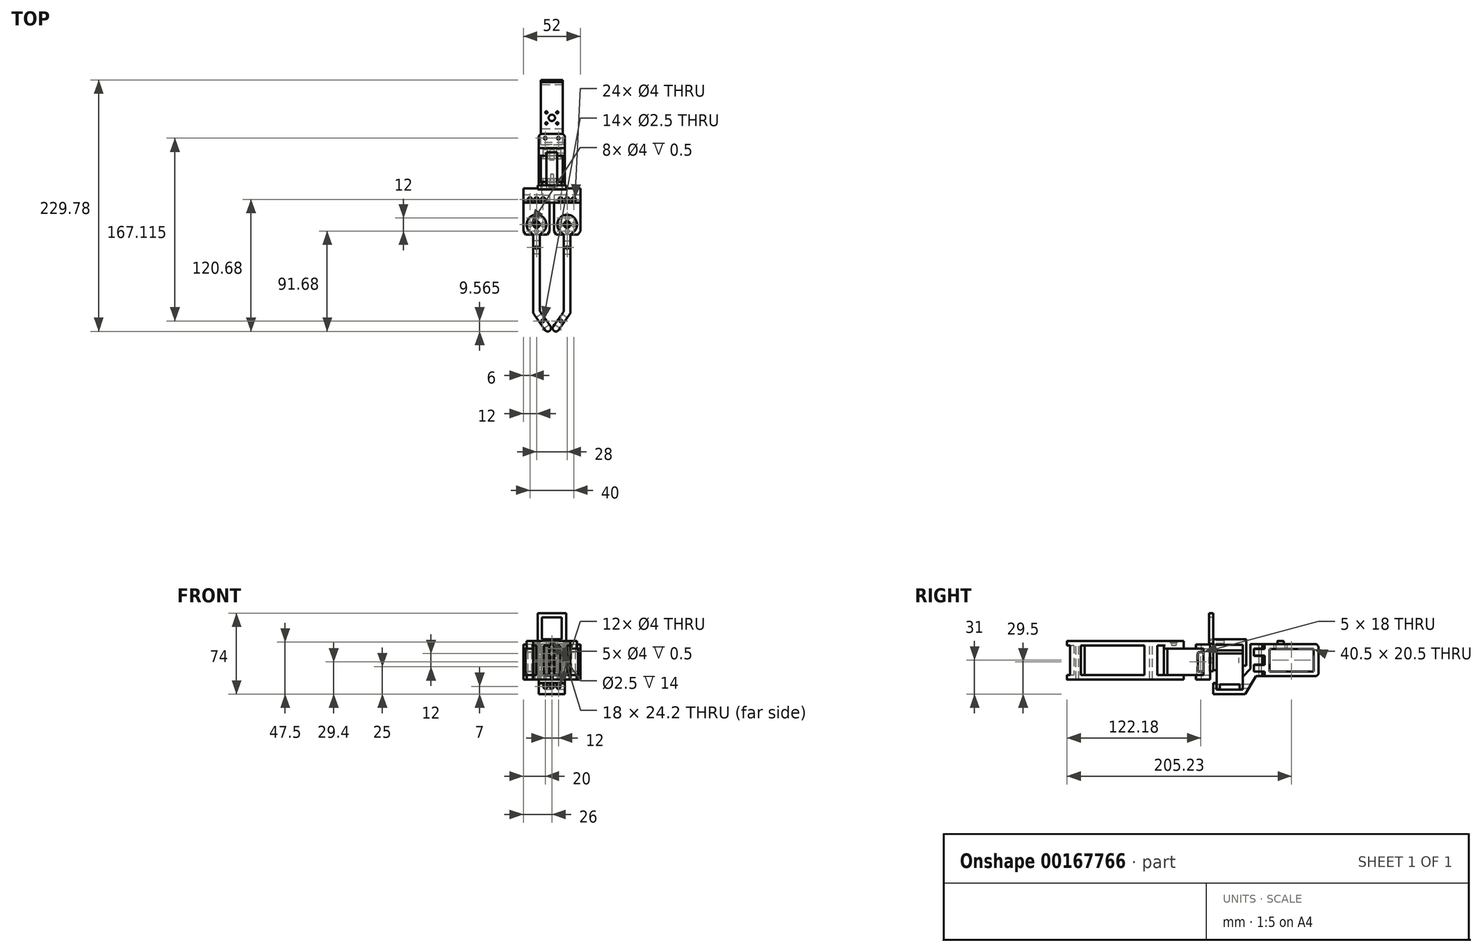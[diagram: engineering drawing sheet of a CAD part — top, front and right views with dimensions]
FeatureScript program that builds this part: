
annotation { "Feature Type Name" : "Feature", "Feature Type Description" : "" }
export const myFeature = defineFeature(function(context is Context, id is Id, definition is map)
    precondition{}
    {
        {
            var Q0;
            Q0=qCreatedBy(makeId("Right.planeOp"),FACE);
            var sketch = newSketch(context, id + "F0", { "sketchPlane" : qUnion([Q0])});
            skLineSegment(sketch, "E0.bottom", {"start": v(30.25, 10.25) * mm, "end": v(-10.25, 10.25) * mm});
            skLineSegment(sketch, "E0.top", {"start": v(30.25, -10.25) * mm, "end": v(-10.25, -10.25) * mm});
            skLineSegment(sketch, "E0.left", {"start": v(30.25, 10.25) * mm, "end": v(30.25, -10.25) * mm});
            skLineSegment(sketch, "E0.right", {"start": v(-10.25, 10.25) * mm, "end": v(-10.25, -10.25) * mm});
            skLineSegment(sketch, "E1.bottom", {"start": v(-14.55, 14.55) * mm, "end": v(34.55, 14.55) * mm});
            skLineSegment(sketch, "E1.top", {"start": v(-14.55, -14.55) * mm, "end": v(34.55, -14.55) * mm});
            skLineSegment(sketch, "E1.left", {"start": v(-14.55, 14.55) * mm, "end": v(-14.55, -14.55) * mm});
            skLineSegment(sketch, "E1.right", {"start": v(34.55, 14.55) * mm, "end": v(34.55, -14.55) * mm});
            skLineSegment(sketch, "E2", {"start": v(10, 14.55) * mm, "end": v(10, 10.25) * mm, "construction": true});
            skLineSegment(sketch, "E3", {"start": v(30.25, 0) * mm, "end": v(34.55, 0) * mm, "construction": true});
            skLineSegment(sketch, "E4", {"start": v(-10.25, 0) * mm, "end": v(10.25, 0) * mm, "construction": true});
            skSolve(sketch);
        }
        {
            var Q0;
            Q0=qSketchRegion(id+"F0",true);
            extrude(context, id + "F1", {"entities" : qUnion([Q0]), "endBound" : BoundingType.SYMMETRIC, "depth" : 20 * mm});
        }
        {
            var Q0;
            Q0=makeQuery(id+"F1.opExtrude","SWEPT_EDGE",EDGE,{"disambiguationData":[OSD([sQuery(id+"F0.wireOp",EDGE,"E1.bottom"),sQuery(id+"F0.wireOp",EDGE,"E1.right")])]});
            var Q1;
            Q1=makeQuery(id+"F1.opExtrude","SWEPT_EDGE",EDGE,{"disambiguationData":[OSD([sQuery(id+"F0.wireOp",EDGE,"E1.top"),sQuery(id+"F0.wireOp",EDGE,"E1.right")])]});
            chamfer(context, id + "F2", {"entities" : qUnion([Q0, Q1]), "width" : 2 * mm, "tangentPropagation" : true});
        }
        {
            var Q0;
            Q0=makeQuery(id+"F1.opExtrude","SWEPT_FACE",FACE,{"disambiguationData":[OSD([sQuery(id+"F0.wireOp",EDGE,"E1.bottom")])]});
            var sketch = newSketch(context, id + "F3", { "sketchPlane" : qUnion([Q0])});
            skCircle(sketch, "E5", {"center": v(0, 0) * mm, "radius": 2.9 * mm});
            skSolve(sketch);
        }
        {
            var Q0;
            Q0=qSketchRegion(id+"F3",true);
            extrude(context, id + "F4", {"entities" : qUnion([Q0]), "operationType" : NewBodyOperationType.ADD, "depth" : 3 * mm});
        }
        {
            var Q0;
            Q0=makeQuery(id+"F1.opExtrude","SWEPT_FACE",FACE,{"disambiguationData":[OSD([sQuery(id+"F0.wireOp",EDGE,"E1.left")])]});
            var sketch = newSketch(context, id + "F5", { "sketchPlane" : qUnion([Q0])});
            skLineSegment(sketch, "E6.bottom", {"start": v(-10, 10.25) * mm, "end": v(10, 10.25) * mm});
            skLineSegment(sketch, "E6.top", {"start": v(-10, 4.25) * mm, "end": v(10, 4.25) * mm});
            skLineSegment(sketch, "E6.left", {"start": v(-10, 10.25) * mm, "end": v(-10, 4.25) * mm});
            skLineSegment(sketch, "E6.right", {"start": v(10, 10.25) * mm, "end": v(10, 4.25) * mm});
            skLineSegment(sketch, "E7.bottom", {"start": v(-10, -4.25) * mm, "end": v(10, -4.25) * mm});
            skLineSegment(sketch, "E7.top", {"start": v(-10, -10.25) * mm, "end": v(10, -10.25) * mm});
            skLineSegment(sketch, "E7.left", {"start": v(-10, -4.25) * mm, "end": v(-10, -10.25) * mm});
            skLineSegment(sketch, "E7.right", {"start": v(10, -4.25) * mm, "end": v(10, -10.25) * mm});
            skSolve(sketch);
        }
        {
            var Q0;
            Q0=qSketchRegion(id+"F5",true);
            extrude(context, id + "F6", {"entities" : qUnion([Q0]), "operationType" : NewBodyOperationType.ADD, "depth" : 10 * mm});
        }
        {
            var Q0;
            Q0=qCreatedBy(makeId("Top.planeOp"),FACE);
            var sketch = newSketch(context, id + "F7", { "sketchPlane" : qUnion([Q0])});
            skCircle(sketch, "E8", {"center": v(-6, -18.55) * mm, "radius": 1.25 * mm});
            skCircle(sketch, "E9", {"center": v(6, -18.55) * mm, "radius": 1.25 * mm});
            skSolve(sketch);
        }
        {
            var Q0;
            Q0=qSketchRegion(id+"F7",true);
            extrude(context, id + "F8", {"entities" : qUnion([Q0]), "operationType" : NewBodyOperationType.REMOVE, "endBound" : BoundingType.THROUGH_ALL, "oppositeDirection" : true, "depth" : 25 * mm, "hasSecondDirection" : true, "secondDirectionBound" : SecondDirectionBoundingType.THROUGH_ALL, "secondDirectionOppositeDirection" : false, "secondDirectionDepth" : 25 * mm});
        }
        {
            var Q0;
            Q0=makeQuery(id+"F1.opExtrude","SWEPT_FACE",FACE,{"disambiguationData":[OSD([sQuery(id+"F0.wireOp",EDGE,"E1.bottom")])]});
            var sketch = newSketch(context, id + "F9", { "sketchPlane" : qUnion([Q0])});
            skCircle(sketch, "E10", {"center": v(-5, -5) * mm, "radius": 1 * mm});
            skLineSegment(sketch, "E11.bottom", {"start": v(-5, -5) * mm, "end": v(5, -5) * mm, "construction": true});
            skLineSegment(sketch, "E11.top", {"start": v(-5, 5) * mm, "end": v(5, 5) * mm, "construction": true});
            skLineSegment(sketch, "E11.left", {"start": v(-5, -5) * mm, "end": v(-5, 5) * mm, "construction": true});
            skLineSegment(sketch, "E11.right", {"start": v(5, -5) * mm, "end": v(5, 5) * mm, "construction": true});
            skLineSegment(sketch, "E12", {"start": v(-5, 5) * mm, "end": v(5, -5) * mm, "construction": true});
            skCircle(sketch, "E13", {"center": v(-5, 5) * mm, "radius": 1 * mm});
            skCircle(sketch, "E14", {"center": v(5, 5) * mm, "radius": 1 * mm});
            skCircle(sketch, "E15", {"center": v(5, -5) * mm, "radius": 1 * mm});
            skSolve(sketch);
        }
        {
            var Q0;
            Q0=qSketchRegion(id+"F9",true);
            extrude(context, id + "F10", {"entities" : qUnion([Q0]), "operationType" : NewBodyOperationType.REMOVE, "endBound" : BoundingType.UP_TO_NEXT, "oppositeDirection" : true, "depth" : 25 * mm});
        }
        {
            var Q0;
            Q0=qCreatedBy(makeId("Right.planeOp"),FACE);
            var sketch = newSketch(context, id + "F11", { "sketchPlane" : qUnion([Q0])});
            skLineSegment(sketch, "E16.bottom", {"start": v(-34.55, -27) * mm, "end": v(-58.55, -27) * mm});
            skLineSegment(sketch, "E16.top", {"start": v(-34.55, 9) * mm, "end": v(-58.55, 9) * mm});
            skLineSegment(sketch, "E16.left", {"start": v(-34.55, -27) * mm, "end": v(-34.55, 9) * mm});
            skLineSegment(sketch, "E16.right", {"start": v(-58.55, -27) * mm, "end": v(-58.55, 9) * mm});
            skLineSegment(sketch, "E17.bottom", {"start": v(-58.55, -9) * mm, "end": v(-61.55, -9) * mm, "construction": true});
            skLineSegment(sketch, "E17.top", {"start": v(-58.55, 9) * mm, "end": v(-61.55, 9) * mm, "construction": true});
            skLineSegment(sketch, "E17.left", {"start": v(-58.55, -9) * mm, "end": v(-58.55, 9) * mm, "construction": true});
            skLineSegment(sketch, "E17.right", {"start": v(-61.55, -9) * mm, "end": v(-61.55, 9) * mm, "construction": true});
            skLineSegment(sketch, "E18.bottom", {"start": v(-55.55, -27) * mm, "end": v(-37.55, -27) * mm});
            skLineSegment(sketch, "E18.top", {"start": v(-55.55, -22) * mm, "end": v(-37.55, -22) * mm});
            skLineSegment(sketch, "E18.left", {"start": v(-55.55, -27) * mm, "end": v(-55.55, -22) * mm});
            skLineSegment(sketch, "E18.right", {"start": v(-37.55, -27) * mm, "end": v(-37.55, -22) * mm});
            skSolve(sketch);
        }
        {
            var Q0;
            Q0=makeQuery(id+"F11.imprint","IMPRINT",FACE,{"disambiguationData":[TD([[makeQuery(id+"F11.imprint","IMPRINT",EDGE,{"derivedFrom":sQuery(id+"F11.wireOp",EDGE,"E16.top")}),1.0]])]});
            extrude(context, id + "F12", {"entities" : qUnion([Q0]), "endBound" : BoundingType.SYMMETRIC, "depth" : 24 * mm});
        }
        {
            var Q0;
            Q0=makeQuery(id+"F12.opExtrude","SWEPT_FACE",FACE,{"disambiguationData":[OSD([sQuery(id+"F11.wireOp",EDGE,"E16.right")])]});
            var sketch = newSketch(context, id + "F13", { "sketchPlane" : qUnion([Q0])});
            skCircle(sketch, "E19", {"center": v(0, 0) * mm, "radius": 9 * mm});
            skCircle(sketch, "E20", {"center": v(0, 0) * mm, "radius": 6 * mm, "construction": true});
            skCircle(sketch, "E21", {"center": v(0, 6) * mm, "radius": 2 * mm});
            skCircle(sketch, "E22", {"center": v(6, 0) * mm, "radius": 2 * mm});
            skCircle(sketch, "E23", {"center": v(-6, 0) * mm, "radius": 2 * mm});
            skCircle(sketch, "E24", {"center": v(0, -6) * mm, "radius": 2 * mm});
            skSolve(sketch);
        }
        {
            var Q0;
            Q0 = qSketchRegion(id + "F13", true);
            extrude(context, id + "F14", {"entities" : qUnion([Q0]), "operationType" : NewBodyOperationType.ADD, "depth" : 3 * mm});
        }
        {
            var Q0;
            Q0=makeQuery(id+"F12.opExtrude","CAP_EDGE",EDGE,{"disambiguationData":[OSD([sQuery(id+"F11.wireOp",EDGE,"E16.top")])],"isStart":false});
            var Q1;
            Q1=makeQuery(id+"F12.opExtrude","CAP_EDGE",EDGE,{"disambiguationData":[OSD([sQuery(id+"F11.wireOp",EDGE,"E16.top")])],"isStart":true});
            chamfer(context, id + "F15", {"entities" : qUnion([Q0, Q1]), "chamferType" : ChamferType.TWO_OFFSETS, "width1" : 3 * mm, "oppositeDirection" : false, "width2" : 2 * mm, "tangentPropagation" : true});
        }
        {
            var Q0;
            Q0=makeQuery(id+"F12.opExtrude","SWEPT_FACE",FACE,{"disambiguationData":[OSD([sQuery(id+"F11.wireOp",EDGE,"E16.left")])]});
            var sketch = newSketch(context, id + "F16", { "sketchPlane" : qUnion([Q0])});
            skCircle(sketch, "E25", {"center": v(0, 0) * mm, "radius": 2 * mm});
            skSolve(sketch);
        }
        {
            var Q0;
            Q0 = qSketchRegion(id + "F16", true);
            extrude(context, id + "F17", {"entities" : qUnion([Q0]), "operationType" : NewBodyOperationType.REMOVE, "oppositeDirection" : true, "depth" : 4 * mm});
        }
        {
            var Q0;
            Q0=qCreatedBy(makeId("Right.planeOp"),FACE);
            var sketch = newSketch(context, id + "F18", { "sketchPlane" : qUnion([Q0])});
            skLineSegment(sketch, "E26", {"start": v(-14.55, 14.55) * mm, "end": v(-14.55, 10.45) * mm});
            skLineSegment(sketch, "E27", {"start": v(-14.55, 10.45) * mm, "end": v(-24.55, 10.45) * mm});
            skLineSegment(sketch, "E28", {"start": v(-24.55, 10.45) * mm, "end": v(-24.55, 4.05) * mm});
            skLineSegment(sketch, "E29", {"start": v(-24.55, 4.05) * mm, "end": v(-14.55, 4.05) * mm});
            skLineSegment(sketch, "E30", {"start": v(-14.55, 4.05) * mm, "end": v(-14.55, -4.05) * mm});
            skLineSegment(sketch, "E31", {"start": v(-14.55, -4.05) * mm, "end": v(-24.55, -4.05) * mm});
            skLineSegment(sketch, "E32", {"start": v(-24.55, -4.05) * mm, "end": v(-24.55, -10.45) * mm});
            skLineSegment(sketch, "E33", {"start": v(-24.55, -10.45) * mm, "end": v(-14.55, -10.45) * mm});
            skLineSegment(sketch, "E34", {"start": v(-14.55, -10.45) * mm, "end": v(-14.55, -14.55) * mm});
            skLineSegment(sketch, "E35", {"start": v(-14.55, -14.55) * mm, "end": v(-22.55, -14.55) * mm});
            skLineSegment(sketch, "E36", {"start": v(-22.55, -14.55) * mm, "end": v(-32.27, -31) * mm});
            skLineSegment(sketch, "E37", {"start": v(-32.27, -31) * mm, "end": v(-61.75, -31) * mm});
            skLineSegment(sketch, "E38", {"start": v(-61.75, -31) * mm, "end": v(-61.75, -21) * mm});
            skLineSegment(sketch, "E39", {"start": v(-61.75, -21) * mm, "end": v(-58.75, -21) * mm});
            skLineSegment(sketch, "E40", {"start": v(-58.75, -21) * mm, "end": v(-58.75, -27) * mm});
            skLineSegment(sketch, "E41", {"start": v(-58.75, -27) * mm, "end": v(-34.55, -27) * mm});
            skLineSegment(sketch, "E42", {"start": v(-34.55, -27) * mm, "end": v(-34.55, -15) * mm});
            skLineSegment(sketch, "E43", {"start": v(-34.55, -15) * mm, "end": v(-27.55, -8) * mm});
            skLineSegment(sketch, "E44", {"start": v(-27.55, -8) * mm, "end": v(-27.55, 14.55) * mm});
            skLineSegment(sketch, "E45", {"start": v(-27.55, 14.55) * mm, "end": v(-14.55, 14.55) * mm});
            skCircle(sketch, "E46", {"center": v(-34.55, -27) * mm, "radius": 4 * mm, "construction": true});
            skSolve(sketch);
        }
        {
            var Q0;
            Q0 = qSketchRegion(id + "F18", true);
            extrude(context, id + "F19", {"entities" : qUnion([Q0]), "endBound" : BoundingType.SYMMETRIC, "depth" : 24 * mm});
        }
        {
            var Q0;
            Q0=makeQuery(id+"F19.opExtrude","CAP_EDGE",EDGE,{"disambiguationData":[OSD([sQuery(id+"F18.wireOp",EDGE,"E26")])],"isStart":false});
            var Q1;
            Q1=makeQuery(id+"F19.opExtrude","CAP_EDGE",EDGE,{"disambiguationData":[OSD([sQuery(id+"F18.wireOp",EDGE,"E30")])],"isStart":false});
            var Q2;
            Q2=makeQuery(id+"F19.opExtrude","CAP_EDGE",EDGE,{"disambiguationData":[OSD([sQuery(id+"F18.wireOp",EDGE,"E34")])],"isStart":false});
            var Q3;
            Q3=makeQuery(id+"F19.opExtrude","CAP_EDGE",EDGE,{"disambiguationData":[OSD([sQuery(id+"F18.wireOp",EDGE,"E26")])],"isStart":true});
            var Q4;
            Q4=makeQuery(id+"F19.opExtrude","CAP_EDGE",EDGE,{"disambiguationData":[OSD([sQuery(id+"F18.wireOp",EDGE,"E30")])],"isStart":true});
            var Q5;
            Q5=makeQuery(id+"F19.opExtrude","CAP_EDGE",EDGE,{"disambiguationData":[OSD([sQuery(id+"F18.wireOp",EDGE,"E34")])],"isStart":true});
            chamfer(context, id + "F20", {"entities" : qUnion([Q0, Q1, Q2, Q3, Q4, Q5]), "width" : 2 * mm, "tangentPropagation" : true});
        }
        {
            var Q0;
            Q0 = qSketchRegion(id + "F7", true);
            extrude(context, id + "F21", {"entities" : qUnion([Q0]), "operationType" : NewBodyOperationType.REMOVE, "endBound" : BoundingType.THROUGH_ALL, "oppositeDirection" : true, "depth" : 25 * mm, "hasSecondDirection" : true, "secondDirectionBound" : SecondDirectionBoundingType.THROUGH_ALL, "secondDirectionOppositeDirection" : false, "secondDirectionDepth" : 25 * mm});
        }
        {
            var Q0;
            Q0=makeQuery(id+"F19.opExtrude","SWEPT_FACE",FACE,{"disambiguationData":[OSD([sQuery(id+"F18.wireOp",EDGE,"E42")])]});
            var sketch = newSketch(context, id + "F22", { "sketchPlane" : qUnion([Q0])});
            skCircle(sketch, "E47", {"center": v(0, -24) * mm, "radius": 2 * mm});
            skPoint(sketch, "E47.centerSnap0", {"position": v(0, -27) * mm});
            skCircle(sketch, "E48", {"center": v(6, -24) * mm, "radius": 2 * mm});
            skCircle(sketch, "E49", {"center": v(-6, -24) * mm, "radius": 2 * mm});
            skSolve(sketch);
        }
        {
            var Q0;
            Q0 = qSketchRegion(id + "F22", true);
            extrude(context, id + "F23", {"entities" : qUnion([Q0]), "operationType" : NewBodyOperationType.REMOVE, "endBound" : BoundingType.THROUGH_ALL, "oppositeDirection" : true, "depth" : 25 * mm, "hasSecondDirection" : true, "secondDirectionBound" : SecondDirectionBoundingType.THROUGH_ALL, "secondDirectionOppositeDirection" : false, "secondDirectionDepth" : 25 * mm});
        }
        {
            var Q0;
            Q0=qCreatedBy(makeId("Right.planeOp"),FACE);
            var sketch = newSketch(context, id + "F24", { "sketchPlane" : qUnion([Q0])});
            skLineSegment(sketch, "E50", {"start": v(-31.55, 19) * mm, "end": v(-31.55, -5) * mm});
            skLineSegment(sketch, "E51", {"start": v(-31.55, -5) * mm, "end": v(-34.55, -5) * mm});
            skLineSegment(sketch, "E52", {"start": v(-34.55, -5) * mm, "end": v(-34.55, 14) * mm});
            skLineSegment(sketch, "E53", {"start": v(-34.55, 14) * mm, "end": v(-61.55, 14) * mm});
            skLineSegment(sketch, "E54", {"start": v(-61.55, 14) * mm, "end": v(-61.55, 19) * mm});
            skLineSegment(sketch, "E55", {"start": v(-61.55, 19) * mm, "end": v(-31.55, 19) * mm});
            skSolve(sketch);
        }
        {
            var Q0;
            Q0 = qSketchRegion(id + "F24", true);
            extrude(context, id + "F25", {"entities" : qUnion([Q0]), "endBound" : BoundingType.SYMMETRIC, "depth" : 10 * mm});
        }
        {
            var Q0;
            Q0=makeQuery(id+"F25.opExtrude","SWEPT_FACE",FACE,{"disambiguationData":[OSD([sQuery(id+"F24.wireOp",EDGE,"E52")])]});
            var sketch = newSketch(context, id + "F26", { "sketchPlane" : qUnion([Q0])});
            skCircle(sketch, "E56", {"center": v(0, 0) * mm, "radius": 2 * mm});
            skSolve(sketch);
        }
        {
            var Q0;
            Q0 = qSketchRegion(id + "F26", true);
            extrude(context, id + "F27", {"entities" : qUnion([Q0]), "operationType" : NewBodyOperationType.ADD, "depth" : 3.5 * mm});
        }
        {
            var Q0;
            Q0=makeQuery(id+"F25.opExtrude","SWEPT_FACE",FACE,{"disambiguationData":[OSD([sQuery(id+"F24.wireOp",EDGE,"E54")])]});
            var sketch = newSketch(context, id + "F28", { "sketchPlane" : qUnion([Q0])});
            skCircle(sketch, "E57", {"center": v(0, 16.5) * mm, "radius": 1.25 * mm});
            skSolve(sketch);
        }
        {
            var Q0;
            Q0 = qSketchRegion(id + "F28", true);
            extrude(context, id + "F29", {"entities" : qUnion([Q0]), "operationType" : NewBodyOperationType.REMOVE, "oppositeDirection" : true, "depth" : 10 * mm});
        }
        {
            var Q0;
            Q0=makeQuery(id+"F25.opExtrude","CAP_EDGE",EDGE,{"disambiguationData":[OSD([sQuery(id+"F24.wireOp",EDGE,"E51")])],"isStart":false});
            var Q1;
            Q1=makeQuery(id+"F25.opExtrude","CAP_EDGE",EDGE,{"disambiguationData":[OSD([sQuery(id+"F24.wireOp",EDGE,"E51")])],"isStart":true});
            fillet(context, id + "F30", {"entities" : qUnion([Q0, Q1]), "radius" : 5 * mm, "tangentPropagation" : true});
        }
        {
            var Q0;
            Q0=makeQuery(id+"F14.opExtrude","CAP_FACE",FACE,{"disambiguationData":[OSD([sQuery(id+"F13.wireOp",EDGE,"E19"),sQuery(id+"F13.wireOp",EDGE,"E21"),sQuery(id+"F13.wireOp",EDGE,"E22"),sQuery(id+"F13.wireOp",EDGE,"E23"),sQuery(id+"F13.wireOp",EDGE,"E24")])],"isStart":false});
            var sketch = newSketch(context, id + "F31", { "sketchPlane" : qUnion([Q0])});
            skLineSegment(sketch, "E58.0", {"start": v(5, 19) * mm, "end": v(-5, 19) * mm});
            skLineSegment(sketch, "E59", {"start": v(-5, 19) * mm, "end": v(-5, 9.14) * mm});
            skLineSegment(sketch, "E60", {"start": v(-5, 9.14) * mm, "end": v(-10, 4.14) * mm});
            skLineSegment(sketch, "E61", {"start": v(-10, 4.14) * mm, "end": v(-10, -10) * mm});
            skLineSegment(sketch, "E62", {"start": v(-10, -10) * mm, "end": v(10, -10) * mm});
            skLineSegment(sketch, "E63", {"start": v(10, -10) * mm, "end": v(10, 4.14) * mm});
            skLineSegment(sketch, "E64", {"start": v(10, 4.14) * mm, "end": v(5, 9.14) * mm});
            skLineSegment(sketch, "E65", {"start": v(5, 9.14) * mm, "end": v(5, 19) * mm});
            skCircle(sketch, "E66", {"center": v(0, 0) * mm, "radius": 10 * mm, "construction": true});
            skCircle(sketch, "E67.0", {"center": v(0, 16.5) * mm, "radius": 1.25 * mm});
            skCircle(sketch, "E68", {"center": v(0, 0) * mm, "radius": 2 * mm});
            skSolve(sketch);
        }
        {
            var Q0;
            Q0 = qSketchRegion(id + "F31", true);
            extrude(context, id + "F32", {"entities" : qUnion([Q0]), "depth" : 4 * mm});
        }
        {
            var Q0;
            Q0=makeQuery(id+"F32.opExtrude","SWEPT_EDGE",EDGE,{"disambiguationData":[OSD([sQuery(id+"F31.wireOp",EDGE,"E62"),sQuery(id+"F31.wireOp",EDGE,"E63")])]});
            var Q1;
            Q1=makeQuery(id+"F32.opExtrude","SWEPT_EDGE",EDGE,{"disambiguationData":[OSD([sQuery(id+"F31.wireOp",EDGE,"E61"),sQuery(id+"F31.wireOp",EDGE,"E62")])]});
            var Q2;
            Q2=makeQuery(id+"F32.opExtrude","SWEPT_EDGE",EDGE,{"disambiguationData":[OSD([sQuery(id+"F31.wireOp",EDGE,"E63"),sQuery(id+"F31.wireOp",EDGE,"E64")])]});
            var Q3;
            Q3=makeQuery(id+"F32.opExtrude","SWEPT_EDGE",EDGE,{"disambiguationData":[OSD([sQuery(id+"F31.wireOp",EDGE,"E60"),sQuery(id+"F31.wireOp",EDGE,"E61")])]});
            fillet(context, id + "F33", {"entities" : qUnion([Q0, Q1, Q2, Q3]), "radius" : 10 * mm});
        }
        {
            var Q0;
            Q0=makeQuery(id+"F32.opExtrude","CAP_FACE",FACE,{"disambiguationData":[OSD([sQuery(id+"F31.wireOp",EDGE,"E58.0"),sQuery(id+"F31.wireOp",EDGE,"E59"),sQuery(id+"F31.wireOp",EDGE,"E60"),sQuery(id+"F31.wireOp",EDGE,"E61"),sQuery(id+"F31.wireOp",EDGE,"E62"),sQuery(id+"F31.wireOp",EDGE,"E63"),sQuery(id+"F31.wireOp",EDGE,"E64"),sQuery(id+"F31.wireOp",EDGE,"E65"),sQuery(id+"F31.wireOp",EDGE,"E67.0")])],"isStart":true});
            var sketch = newSketch(context, id + "F34", { "sketchPlane" : qUnion([Q0])});
            skCircle(sketch, "E69.0", {"center": v(0, 6) * mm, "radius": 2 * mm});
            skCircle(sketch, "E69.1", {"center": v(6, 0) * mm, "radius": 2 * mm});
            skCircle(sketch, "E69.2", {"center": v(-6, 0) * mm, "radius": 2 * mm});
            skCircle(sketch, "E69.3", {"center": v(0, -6) * mm, "radius": 2 * mm});
            skSolve(sketch);
        }
        {
            var Q0;
            Q0 = qSketchRegion(id + "F34", true);
            extrude(context, id + "F35", {"entities" : qUnion([Q0]), "operationType" : NewBodyOperationType.ADD, "depth" : 2.5 * mm});
        }
        {
            var Q0;
            Q0=makeQuery(id+"F32.opExtrude","CAP_FACE",FACE,{"disambiguationData":[OSD([sQuery(id+"F31.wireOp",EDGE,"E58.0"),sQuery(id+"F31.wireOp",EDGE,"E59"),sQuery(id+"F31.wireOp",EDGE,"E60"),sQuery(id+"F31.wireOp",EDGE,"E61"),sQuery(id+"F31.wireOp",EDGE,"E62"),sQuery(id+"F31.wireOp",EDGE,"E63"),sQuery(id+"F31.wireOp",EDGE,"E64"),sQuery(id+"F31.wireOp",EDGE,"E65"),sQuery(id+"F31.wireOp",EDGE,"E67.0"),sQuery(id+"F31.wireOp",EDGE,"E68")])],"isStart":false});
            var sketch = newSketch(context, id + "F36", { "sketchPlane" : qUnion([Q0])});
            skCircle(sketch, "E70", {"center": v(0, 0) * mm, "radius": 3 * mm});
            skSolve(sketch);
        }
        {
            var Q0;
            Q0 = qSketchRegion(id + "F36", true);
            extrude(context, id + "F37", {"entities" : qUnion([Q0]), "operationType" : NewBodyOperationType.REMOVE, "oppositeDirection" : true, "depth" : 2 * mm});
        }
        {
            var Q0;
            Q0=makeQuery(id+"F32.opExtrude","CAP_FACE",FACE,{"disambiguationData":[OSD([sQuery(id+"F31.wireOp",EDGE,"E58.0"),sQuery(id+"F31.wireOp",EDGE,"E59"),sQuery(id+"F31.wireOp",EDGE,"E60"),sQuery(id+"F31.wireOp",EDGE,"E61"),sQuery(id+"F31.wireOp",EDGE,"E62"),sQuery(id+"F31.wireOp",EDGE,"E63"),sQuery(id+"F31.wireOp",EDGE,"E64"),sQuery(id+"F31.wireOp",EDGE,"E65"),sQuery(id+"F31.wireOp",EDGE,"E67.0"),sQuery(id+"F31.wireOp",EDGE,"E68")])],"isStart":false});
            var sketch = newSketch(context, id + "F38", { "sketchPlane" : qUnion([Q0])});
            skLineSegment(sketch, "E71.bottom", {"start": v(-9, 19) * mm, "end": v(9, 19) * mm});
            skLineSegment(sketch, "E71.top", {"start": v(-9, 39) * mm, "end": v(9, 39) * mm});
            skLineSegment(sketch, "E71.left", {"start": v(-9, 19) * mm, "end": v(-9, 39) * mm});
            skLineSegment(sketch, "E71.right", {"start": v(9, 19) * mm, "end": v(9, 39) * mm});
            skLineSegment(sketch, "E72.bottom", {"start": v(13, 43) * mm, "end": v(-13, 43) * mm});
            skLineSegment(sketch, "E72.top", {"start": v(13, 15) * mm, "end": v(-13, 15) * mm, "construction": true});
            skLineSegment(sketch, "E72.left", {"start": v(13, 43) * mm, "end": v(13, 15) * mm});
            skLineSegment(sketch, "E72.right", {"start": v(-13, 43) * mm, "end": v(-13, 15) * mm});
            skLineSegment(sketch, "E73", {"start": v(-13, 15) * mm, "end": v(-5, 15) * mm});
            skLineSegment(sketch, "E74", {"start": v(-5, 15) * mm, "end": v(-5, 19) * mm});
            skLineSegment(sketch, "E75", {"start": v(13, 15) * mm, "end": v(5, 15) * mm});
            skLineSegment(sketch, "E76", {"start": v(5, 15) * mm, "end": v(5, 19) * mm});
            skSolve(sketch);
        }
        {
            var Q0;
            Q0=makeQuery(id+"F38.imprint","IMPRINT",FACE,{"disambiguationData":[TD([[makeQuery(id+"F38.imprint","IMPRINT",EDGE,{"derivedFrom":sQuery(id+"F38.wireOp",EDGE,"E71.top")}),1.0]])]});
            var Q1;
            Q1=makeQuery(id+"F32.opExtrude","CAP_FACE",FACE,{"disambiguationData":[OSD([sQuery(id+"F31.wireOp",EDGE,"E58.0"),sQuery(id+"F31.wireOp",EDGE,"E59"),sQuery(id+"F31.wireOp",EDGE,"E60"),sQuery(id+"F31.wireOp",EDGE,"E61"),sQuery(id+"F31.wireOp",EDGE,"E62"),sQuery(id+"F31.wireOp",EDGE,"E63"),sQuery(id+"F31.wireOp",EDGE,"E64"),sQuery(id+"F31.wireOp",EDGE,"E65"),sQuery(id+"F31.wireOp",EDGE,"E67.0"),sQuery(id+"F31.wireOp",EDGE,"E68")])],"isStart":true});
            extrude(context, id + "F39", {"entities" : qUnion([Q0]), "operationType" : NewBodyOperationType.ADD, "endBound" : BoundingType.UP_TO_SURFACE, "oppositeDirection" : true, "endBoundEntityFace" : qUnion([Q1]), "depth" : 25 * mm});
        }
        {
            var Q0;
            Q0=qCreatedBy(makeId("Right.planeOp"),FACE);
            var sketch = newSketch(context, id + "F40", { "sketchPlane" : qUnion([Q0])});
            skLineSegment(sketch, "E77.bottom", {"start": v(-70.55, 10.5) * mm, "end": v(-106.55, 10.5) * mm});
            skLineSegment(sketch, "E77.top", {"start": v(-70.55, -13.5) * mm, "end": v(-106.55, -13.5) * mm});
            skLineSegment(sketch, "E77.left", {"start": v(-70.55, 10.5) * mm, "end": v(-70.55, -13.5) * mm});
            skLineSegment(sketch, "E77.right", {"start": v(-106.55, 10.5) * mm, "end": v(-106.55, -13.5) * mm});
            skLineSegment(sketch, "E78.bottom", {"start": v(-70.55, 7.5) * mm, "end": v(-75.55, 7.5) * mm});
            skLineSegment(sketch, "E78.top", {"start": v(-70.55, -10.5) * mm, "end": v(-75.55, -10.5) * mm});
            skLineSegment(sketch, "E78.left", {"start": v(-70.55, 7.5) * mm, "end": v(-70.55, -10.5) * mm});
            skLineSegment(sketch, "E78.right", {"start": v(-75.55, 7.5) * mm, "end": v(-75.55, -10.5) * mm});
            skLineSegment(sketch, "E79.bottom", {"start": v(-106.55, 10.5) * mm, "end": v(-88.55, 10.5) * mm, "construction": true});
            skLineSegment(sketch, "E79.top", {"start": v(-106.55, 13.5) * mm, "end": v(-88.55, 13.5) * mm, "construction": true});
            skLineSegment(sketch, "E79.left", {"start": v(-106.55, 10.5) * mm, "end": v(-106.55, 13.5) * mm, "construction": true});
            skLineSegment(sketch, "E79.right", {"start": v(-88.55, 10.5) * mm, "end": v(-88.55, 13.5) * mm, "construction": true});
            skSolve(sketch);
        }
        {
            var Q0;
            {var subQ4=sQuery(id+"F40.wireOp",EDGE,"E77.bottom");Q0=makeQuery(id+"F40.imprint","IMPRINT",FACE,{"disambiguationData":[TD([[makeQuery(id+"F40.imprint","IMPRINT",EDGE,{"derivedFrom":subQ4}),1.0]])]});}
            extrude(context, id + "F41", {"entities" : qUnion([Q0]), "depth" : 26 * mm, "hasSecondDirection" : true, "secondDirectionOppositeDirection" : false, "secondDirectionDepth" : 2 * mm});
        }
        {
            var Q0;
            Q0=makeQuery(id+"F41.opExtrude","SWEPT_FACE",FACE,{"disambiguationData":[OSD([sQuery(id+"F40.wireOp",EDGE,"E77.bottom")])]});
            var sketch = newSketch(context, id + "F42", { "sketchPlane" : qUnion([Q0])});
            skCircle(sketch, "E80", {"center": v(14, -97.55) * mm, "radius": 9 * mm});
            skCircle(sketch, "E81", {"center": v(14, -97.55) * mm, "radius": 6 * mm, "construction": true});
            skCircle(sketch, "E82", {"center": v(14, -91.55) * mm, "radius": 2 * mm});
            skCircle(sketch, "E83", {"center": v(8, -97.55) * mm, "radius": 2 * mm});
            skCircle(sketch, "E84", {"center": v(14, -103.55) * mm, "radius": 2 * mm});
            skCircle(sketch, "E85", {"center": v(20, -97.55) * mm, "radius": 2 * mm});
            skSolve(sketch);
        }
        {
            var Q0;
            Q0 = qSketchRegion(id + "F42", true);
            extrude(context, id + "F43", {"entities" : qUnion([Q0]), "operationType" : NewBodyOperationType.ADD, "depth" : 3 * mm});
        }
        {
            var Q0;
            Q0=makeQuery(id+"F39.boolean.opBoolean","MERGE",FACE,{"derivedFrom":[makeQuery(id+"F32.opExtrude","CAP_FACE",FACE,{"disambiguationData":[OSD([sQuery(id+"F31.wireOp",EDGE,"E58.0"),sQuery(id+"F31.wireOp",EDGE,"E59"),sQuery(id+"F31.wireOp",EDGE,"E60"),sQuery(id+"F31.wireOp",EDGE,"E61"),sQuery(id+"F31.wireOp",EDGE,"E62"),sQuery(id+"F31.wireOp",EDGE,"E63"),sQuery(id+"F31.wireOp",EDGE,"E64"),sQuery(id+"F31.wireOp",EDGE,"E65"),sQuery(id+"F31.wireOp",EDGE,"E67.0"),sQuery(id+"F31.wireOp",EDGE,"E68")])],"isStart":false}),makeQuery(id+"F39.opExtrude","CAP_FACE",FACE,{"disambiguationData":[OSD([sQuery(id+"F38.wireOp",EDGE,"E71.bottom"),sQuery(id+"F38.wireOp",EDGE,"E71.top"),sQuery(id+"F38.wireOp",EDGE,"E71.left"),sQuery(id+"F38.wireOp",EDGE,"E71.right"),sQuery(id+"F38.wireOp",EDGE,"E72.bottom"),sQuery(id+"F38.wireOp",EDGE,"E72.left"),sQuery(id+"F38.wireOp",EDGE,"E72.right"),sQuery(id+"F38.wireOp",EDGE,"E73"),sQuery(id+"F38.wireOp",EDGE,"E74"),sQuery(id+"F38.wireOp",EDGE,"E75"),sQuery(id+"F38.wireOp",EDGE,"E76")])],"isStart":true})]});
            var sketch = newSketch(context, id + "F44", { "sketchPlane" : qUnion([Q0])});
            skLineSegment(sketch, "E86.bottom", {"start": v(-8.9, 10.5) * mm, "end": v(8.9, 10.5) * mm});
            skLineSegment(sketch, "E86.top", {"start": v(-8.9, -13.5) * mm, "end": v(8.9, -13.5) * mm});
            skLineSegment(sketch, "E86.left", {"start": v(-8.9, 10.5) * mm, "end": v(-8.9, -13.5) * mm});
            skLineSegment(sketch, "E86.right", {"start": v(8.9, 10.5) * mm, "end": v(8.9, -13.5) * mm});
            skLineSegment(sketch, "E87.bottom", {"start": v(-25, 14.7) * mm, "end": v(25, 14.7) * mm});
            skLineSegment(sketch, "E87.top", {"start": v(-25, -17.7) * mm, "end": v(25, -17.7) * mm});
            skLineSegment(sketch, "E87.left", {"start": v(-25, 14.7) * mm, "end": v(-25, -17.7) * mm});
            skLineSegment(sketch, "E87.right", {"start": v(25, 14.7) * mm, "end": v(25, -17.7) * mm});
            skSolve(sketch);
        }
        {
            var Q0;
            Q0 = qSketchRegion(id + "F44", true);
            extrude(context, id + "F45", {"entities" : qUnion([Q0]), "operationType" : NewBodyOperationType.REMOVE, "oppositeDirection" : true, "depth" : 1 * mm});
        }
        {
            var Q0;
            {var subQ0=sQuery(id+"F44.wireOp",EDGE,"E86.bottom");var subQ1=sQuery(id+"F44.wireOp",EDGE,"E87.bottom");Q0=makeQuery(id+"F45.boolean.opBoolean","COPY",FACE,{"disambiguationData":[TD([makeQuery(id+"F32.opExtrude","SWEPT_FACE",FACE,{"disambiguationData":[OSD([sQuery(id+"F31.wireOp",EDGE,"E59")])]})])],"derivedFrom":makeQuery(id+"F45.opExtrude","CAP_FACE",FACE,{"disambiguationData":[OSD([subQ0,sQuery(id+"F44.wireOp",EDGE,"E86.top"),sQuery(id+"F44.wireOp",EDGE,"E86.left"),sQuery(id+"F44.wireOp",EDGE,"E86.right"),subQ1,sQuery(id+"F44.wireOp",EDGE,"E87.top"),sQuery(id+"F44.wireOp",EDGE,"E87.left"),sQuery(id+"F44.wireOp",EDGE,"E87.right")])],"isStart":false})});}
            var sketch = newSketch(context, id + "F46", { "sketchPlane" : qUnion([Q0])});
            skLineSegment(sketch, "E88.bottom", {"start": v(-9, 10.5) * mm, "end": v(9, 10.5) * mm});
            skLineSegment(sketch, "E88.top", {"start": v(-9, -13.7) * mm, "end": v(9, -13.7) * mm});
            skLineSegment(sketch, "E88.left", {"start": v(-9, 10.5) * mm, "end": v(-9, -13.7) * mm});
            skLineSegment(sketch, "E88.right", {"start": v(9, 10.5) * mm, "end": v(9, -13.7) * mm});
            skLineSegment(sketch, "E89.bottom", {"start": v(-26, 14.5) * mm, "end": v(26, 14.5) * mm});
            skLineSegment(sketch, "E89.top", {"start": v(-26, -17.7) * mm, "end": v(26, -17.7) * mm});
            skLineSegment(sketch, "E89.left", {"start": v(-26, 14.5) * mm, "end": v(-26, -17.7) * mm});
            skLineSegment(sketch, "E89.right", {"start": v(26, 14.5) * mm, "end": v(26, -17.7) * mm});
            skSolve(sketch);
        }
        {
            var Q0;
            Q0 = qSketchRegion(id + "F46", true);
            var Q1;
            {var subQ0=sQuery(id+"F40.wireOp",EDGE,"E77.left");Q1=makeQuery(id+"F41.opExtrude","SWEPT_FACE",FACE,{"disambiguationData":[OSD([subQ0]),TDD([makeQuery(id+"F40.imprint","IMPRINT",EDGE,{"disambiguationData":[TD([[makeQuery(id+"F40.imprint","INTERSECT",VERTEX,{"derivedFrom":[sQuery(id+"F40.wireOp",EDGE,"E77.bottom"),subQ0]}),-1.0]])],"derivedFrom":subQ0})])]});}
            extrude(context, id + "F47", {"entities" : qUnion([Q0]), "endBound" : BoundingType.UP_TO_SURFACE, "endBoundEntityFace" : qUnion([Q1]), "depth" : 25 * mm});
        }
        {
            var Q0;
            Q0=makeQuery(id+"F47.opExtrude","CAP_FACE",FACE,{"disambiguationData":[OSD([sQuery(id+"F46.wireOp",EDGE,"E88.bottom"),sQuery(id+"F46.wireOp",EDGE,"E88.top"),sQuery(id+"F46.wireOp",EDGE,"E88.left"),sQuery(id+"F46.wireOp",EDGE,"E88.right"),sQuery(id+"F46.wireOp",EDGE,"E89.bottom"),sQuery(id+"F46.wireOp",EDGE,"E89.top"),sQuery(id+"F46.wireOp",EDGE,"E89.left"),sQuery(id+"F46.wireOp",EDGE,"E89.right")])],"isStart":false});
            var sketch = newSketch(context, id + "F48", { "sketchPlane" : qUnion([Q0])});
            skLineSegment(sketch, "E90.bottom", {"start": v(-26, 14.5) * mm, "end": v(26, 14.5) * mm});
            skLineSegment(sketch, "E90.top", {"start": v(-26, 10.5) * mm, "end": v(26, 10.5) * mm});
            skLineSegment(sketch, "E90.left", {"start": v(-26, 14.5) * mm, "end": v(-26, 10.5) * mm});
            skLineSegment(sketch, "E90.right", {"start": v(26, 14.5) * mm, "end": v(26, 10.5) * mm});
            skLineSegment(sketch, "E91.bottom", {"start": v(-26, -17.7) * mm, "end": v(26, -17.7) * mm});
            skLineSegment(sketch, "E91.top", {"start": v(-26, -13.7) * mm, "end": v(26, -13.7) * mm});
            skLineSegment(sketch, "E91.left", {"start": v(-26, -17.7) * mm, "end": v(-26, -13.7) * mm});
            skLineSegment(sketch, "E91.right", {"start": v(26, -17.7) * mm, "end": v(26, -13.7) * mm});
            skSolve(sketch);
        }
        {
            var Q0;
            Q0 = qSketchRegion(id + "F48", true);
            extrude(context, id + "F49", {"entities" : qUnion([Q0]), "operationType" : NewBodyOperationType.ADD, "depth" : 7 * mm});
        }
        {
            var Q0;
            Q0=makeQuery(id+"F49.boolean.opBoolean","MERGE",FACE,{"derivedFrom":[makeQuery(id+"F47.opExtrude","SWEPT_FACE",FACE,{"disambiguationData":[OSD([sQuery(id+"F46.wireOp",EDGE,"E89.bottom")])]}),makeQuery(id+"F49.opExtrude","SWEPT_FACE",FACE,{"disambiguationData":[OSD([sQuery(id+"F48.wireOp",EDGE,"E90.bottom")])]})]});
            var sketch = newSketch(context, id + "F50", { "sketchPlane" : qUnion([Q0])});
            skCircle(sketch, "E92", {"center": v(8, -74.55) * mm, "radius": 2 * mm});
            skCircle(sketch, "E93", {"center": v(14, -74.55) * mm, "radius": 2 * mm});
            skCircle(sketch, "E94", {"center": v(20, -74.55) * mm, "radius": 2 * mm});
            skLineSegment(sketch, "E95", {"start": v(8, -74.55) * mm, "end": v(20, -74.55) * mm, "construction": true});
            skCircle(sketch, "E96.MirrorC", {"center": v(-20, -74.55) * mm, "radius": 2 * mm});
            skCircle(sketch, "E97.MirrorC", {"center": v(-14, -74.55) * mm, "radius": 2 * mm});
            skCircle(sketch, "E98.MirrorC", {"center": v(-8, -74.55) * mm, "radius": 2 * mm});
            skSolve(sketch);
        }
        {
            var Q0;
            Q0 = qSketchRegion(id + "F50", true);
            extrude(context, id + "F51", {"entities" : qUnion([Q0]), "operationType" : NewBodyOperationType.REMOVE, "endBound" : BoundingType.THROUGH_ALL, "oppositeDirection" : true, "depth" : 25 * mm});
        }
        {
            var Q0;
            Q0=makeQuery(id+"F43.opExtrude","CAP_FACE",FACE,{"disambiguationData":[OSD([sQuery(id+"F42.wireOp",EDGE,"E80"),sQuery(id+"F42.wireOp",EDGE,"E82"),sQuery(id+"F42.wireOp",EDGE,"E83"),sQuery(id+"F42.wireOp",EDGE,"E84"),sQuery(id+"F42.wireOp",EDGE,"E85")])],"isStart":false});
            var sketch = newSketch(context, id + "F52", { "sketchPlane" : qUnion([Q0])});
            skCircle(sketch, "E99.0", {"center": v(14, -97.55) * mm, "radius": 9 * mm});
            skLineSegment(sketch, "E100", {"start": v(14, -97.55) * mm, "end": v(14, -177.55) * mm, "construction": true});
            skLineSegment(sketch, "E101", {"start": v(14, -177.55) * mm, "end": v(2, -194.69) * mm, "construction": true});
            skLineSegment(sketch, "E102", {"start": v(11, -106.04) * mm, "end": v(11, -176.6) * mm});
            skLineSegment(sketch, "E103", {"start": v(11, -176.6) * mm, "end": v(-0.46, -192.97) * mm});
            skLineSegment(sketch, "E104", {"start": v(-0.46, -192.97) * mm, "end": v(4.46, -196.4) * mm});
            skLineSegment(sketch, "E105", {"start": v(4.46, -196.4) * mm, "end": v(17, -178.5) * mm});
            skLineSegment(sketch, "E106", {"start": v(17, -178.5) * mm, "end": v(17, -106.04) * mm});
            skCircle(sketch, "E107", {"center": v(14, -97.55) * mm, "radius": 2 * mm});
            skSolve(sketch);
        }
        {
            var Q0;
            Q0 = qSketchRegion(id + "F52", true);
            extrude(context, id + "F53", {"entities" : qUnion([Q0]), "depth" : 4 * mm});
        }
        {
            var Q0;
            Q0=makeQuery(id+"F53.opExtrude","CAP_FACE",FACE,{"disambiguationData":[OSD([sQuery(id+"F52.wireOp",EDGE,"E99.0"),sQuery(id+"F52.wireOp",EDGE,"E102"),sQuery(id+"F52.wireOp",EDGE,"E103"),sQuery(id+"F52.wireOp",EDGE,"E104"),sQuery(id+"F52.wireOp",EDGE,"E105"),sQuery(id+"F52.wireOp",EDGE,"E106")])],"isStart":true});
            var sketch = newSketch(context, id + "F54", { "sketchPlane" : qUnion([Q0])});
            skCircle(sketch, "E108.0", {"center": v(20, 97.55) * mm, "radius": 2 * mm});
            skCircle(sketch, "E108.1", {"center": v(14, 103.55) * mm, "radius": 2 * mm});
            skCircle(sketch, "E108.2", {"center": v(8, 97.55) * mm, "radius": 2 * mm});
            skCircle(sketch, "E108.3", {"center": v(14, 91.55) * mm, "radius": 2 * mm});
            skSolve(sketch);
        }
        {
            var Q0;
            Q0 = qSketchRegion(id + "F54", true);
            extrude(context, id + "F55", {"entities" : qUnion([Q0]), "operationType" : NewBodyOperationType.ADD, "depth" : 2.5 * mm});
        }
        {
            var Q0;
            Q0=makeQuery(id+"F53.opExtrude","CAP_FACE",FACE,{"disambiguationData":[OSD([sQuery(id+"F52.wireOp",EDGE,"E99.0"),sQuery(id+"F52.wireOp",EDGE,"E102"),sQuery(id+"F52.wireOp",EDGE,"E103"),sQuery(id+"F52.wireOp",EDGE,"E104"),sQuery(id+"F52.wireOp",EDGE,"E105"),sQuery(id+"F52.wireOp",EDGE,"E106"),sQuery(id+"F52.wireOp",EDGE,"E107")])],"isStart":false});
            var sketch = newSketch(context, id + "F56", { "sketchPlane" : qUnion([Q0])});
            skCircle(sketch, "E109", {"center": v(14, -97.55) * mm, "radius": 3 * mm});
            skSolve(sketch);
        }
        {
            var Q0;
            Q0 = qSketchRegion(id + "F56", true);
            extrude(context, id + "F57", {"entities" : qUnion([Q0]), "operationType" : NewBodyOperationType.REMOVE, "oppositeDirection" : true, "depth" : 2 * mm});
        }
        {
            var Q0;
            Q0=makeQuery(id+"F53.opExtrude","SWEPT_EDGE",EDGE,{"disambiguationData":[OSD([sQuery(id+"F52.wireOp",EDGE,"E104"),sQuery(id+"F52.wireOp",EDGE,"E105")])]});
            var Q1;
            Q1=makeQuery(id+"F53.opExtrude","SWEPT_EDGE",EDGE,{"disambiguationData":[OSD([sQuery(id+"F52.wireOp",EDGE,"E103"),sQuery(id+"F52.wireOp",EDGE,"E104")])]});
            var Q2;
            Q2=makeQuery(id+"F53.opExtrude","SWEPT_EDGE",EDGE,{"disambiguationData":[OSD([sQuery(id+"F52.wireOp",EDGE,"E105"),sQuery(id+"F52.wireOp",EDGE,"E106")])]});
            var Q3;
            Q3=makeQuery(id+"F53.opExtrude","SWEPT_EDGE",EDGE,{"disambiguationData":[OSD([sQuery(id+"F52.wireOp",EDGE,"E102"),sQuery(id+"F52.wireOp",EDGE,"E103")])]});
            var Q4;
            Q4=makeQuery(id+"F53.opExtrude","SWEPT_EDGE",EDGE,{"disambiguationData":[OSD([sQuery(id+"F52.wireOp",EDGE,"E99.0"),sQuery(id+"F52.wireOp",EDGE,"E106")])]});
            var Q5;
            Q5=makeQuery(id+"F53.opExtrude","SWEPT_EDGE",EDGE,{"disambiguationData":[OSD([sQuery(id+"F52.wireOp",EDGE,"E99.0"),sQuery(id+"F52.wireOp",EDGE,"E102")])]});
            fillet(context, id + "F58", {"entities" : qUnion([Q0, Q1, Q2, Q3, Q4, Q5]), "radius" : 3 * mm, "tangentPropagation" : true});
        }
        {
            var Q0;
            Q0=makeQuery(id+"F41.opExtrude","SWEPT_FACE",FACE,{"disambiguationData":[OSD([sQuery(id+"F40.wireOp",EDGE,"E77.top")])]});
            cPlane(context, id + "F59", {"entities" : qUnion([Q0]), "cplaneType" : CPlaneType.OFFSET, "offset" : 0.2 * mm, "width" : 150 * mm, "height" : 150 * mm});
        }
        {
            var Q0;
            Q0=qCreatedBy(id+"F59.planeOp",FACE);
            var sketch = newSketch(context, id + "F60", { "sketchPlane" : qUnion([Q0])});
            skLineSegment(sketch, "E110.0.0", {"start": v(6.18, 193.95) * mm, "end": v(16.46, 179.27) * mm});
            skArc(sketch, "E110.0.1", {"start": v(16.46, 179.27) * mm, "mid": v(16.86, 178.45) * mm, "end": v(17, 177.55) * mm});
            skLineSegment(sketch, "E110.0.2", {"start": v(17, 177.55) * mm, "end": v(17, 107.94) * mm});
            skArc(sketch, "E110.0.3", {"start": v(17, 107.94) * mm, "mid": v(17.4, 106.44) * mm, "end": v(18.5, 105.34) * mm});
            skArc(sketch, "E110.0.4", {"start": v(18.5, 105.34) * mm, "mid": v(14, 88.55) * mm, "end": v(9.5, 105.34) * mm});
            skArc(sketch, "E110.0.5", {"start": v(9.5, 105.34) * mm, "mid": v(10.6, 106.44) * mm, "end": v(11, 107.94) * mm});
            skLineSegment(sketch, "E110.0.6", {"start": v(11, 107.94) * mm, "end": v(11, 175.66) * mm});
            skArc(sketch, "E110.0.7", {"start": v(11, 175.66) * mm, "mid": v(10.86, 176.56) * mm, "end": v(10.46, 177.38) * mm});
            skLineSegment(sketch, "E110.0.8", {"start": v(10.46, 177.38) * mm, "end": v(1.26, 190.5) * mm});
            skArc(sketch, "E110.0.9", {"start": v(1.26, 190.5) * mm, "mid": v(2, 194.69) * mm, "end": v(6.18, 193.95) * mm});
            skSolve(sketch);
        }
        {
            var Q0;
            Q0 = qSketchRegion(id + "F60", true);
            extrude(context, id + "F61", {"entities" : qUnion([Q0]), "depth" : 4 * mm});
        }
        {
            var Q0;
            Q0=makeQuery(id+"F61.opExtrude","CAP_FACE",FACE,{"disambiguationData":[OSD([sQuery(id+"F60.wireOp",EDGE,"E110.0.0"),sQuery(id+"F60.wireOp",EDGE,"E110.0.1"),sQuery(id+"F60.wireOp",EDGE,"E110.0.2"),sQuery(id+"F60.wireOp",EDGE,"E110.0.3"),sQuery(id+"F60.wireOp",EDGE,"E110.0.4"),sQuery(id+"F60.wireOp",EDGE,"E110.0.5"),sQuery(id+"F60.wireOp",EDGE,"E110.0.6"),sQuery(id+"F60.wireOp",EDGE,"E110.0.7"),sQuery(id+"F60.wireOp",EDGE,"E110.0.8"),sQuery(id+"F60.wireOp",EDGE,"E110.0.9")])],"isStart":true});
            var sketch = newSketch(context, id + "F62", { "sketchPlane" : qUnion([Q0])});
            skCircle(sketch, "E111", {"center": v(14, -97.55) * mm, "radius": 1.95 * mm});
            skSolve(sketch);
        }
        {
            var Q0;
            Q0 = qSketchRegion(id + "F62", true);
            extrude(context, id + "F63", {"entities" : qUnion([Q0]), "operationType" : NewBodyOperationType.ADD, "depth" : 3.5 * mm});
        }
        {
            var Q0;
            Q0=makeQuery(id+"F61.opExtrude","CAP_FACE",FACE,{"disambiguationData":[OSD([sQuery(id+"F60.wireOp",EDGE,"E110.0.0"),sQuery(id+"F60.wireOp",EDGE,"E110.0.1"),sQuery(id+"F60.wireOp",EDGE,"E110.0.2"),sQuery(id+"F60.wireOp",EDGE,"E110.0.3"),sQuery(id+"F60.wireOp",EDGE,"E110.0.4"),sQuery(id+"F60.wireOp",EDGE,"E110.0.5"),sQuery(id+"F60.wireOp",EDGE,"E110.0.6"),sQuery(id+"F60.wireOp",EDGE,"E110.0.7"),sQuery(id+"F60.wireOp",EDGE,"E110.0.8"),sQuery(id+"F60.wireOp",EDGE,"E110.0.9")])],"isStart":true});
            var sketch = newSketch(context, id + "F64", { "sketchPlane" : qUnion([Q0])});
            skLineSegment(sketch, "E112.bottom", {"start": v(11, -112.55) * mm, "end": v(17, -112.55) * mm});
            skLineSegment(sketch, "E112.top", {"start": v(11, -124.55) * mm, "end": v(17, -124.55) * mm});
            skLineSegment(sketch, "E112.left", {"start": v(11, -112.55) * mm, "end": v(11, -124.55) * mm});
            skLineSegment(sketch, "E112.right", {"start": v(17, -112.55) * mm, "end": v(17, -124.55) * mm});
            skLineSegment(sketch, "E113", {"start": v(2.42, -188.86) * mm, "end": v(9.3, -179.03) * mm});
            skLineSegment(sketch, "E114", {"start": v(9.3, -179.03) * mm, "end": v(14.22, -182.47) * mm});
            skLineSegment(sketch, "E115", {"start": v(14.22, -182.47) * mm, "end": v(7.33, -192.3) * mm});
            skLineSegment(sketch, "E116", {"start": v(7.33, -192.3) * mm, "end": v(2.42, -188.86) * mm});
            skLineSegment(sketch, "E117", {"start": v(5.86, -183.94) * mm, "end": v(10.78, -187.39) * mm, "construction": true});
            skCircle(sketch, "E118", {"center": v(14, -97.55) * mm, "radius": 15 * mm, "construction": true});
            skCircle(sketch, "E119", {"center": v(8.32, -185.66) * mm, "radius": 1.25 * mm});
            skCircle(sketch, "E120", {"center": v(14, -118.55) * mm, "radius": 1.25 * mm});
            skLineSegment(sketch, "E121", {"start": v(17, -124.55) * mm, "end": v(11, -112.55) * mm, "construction": true});
            skSolve(sketch);
        }
        {
            var Q0;
            Q0=makeQuery(id+"F64.imprint","IMPRINT",FACE,{"disambiguationData":[TD([[makeQuery(id+"F64.imprint","IMPRINT",EDGE,{"derivedFrom":sQuery(id+"F64.wireOp",EDGE,"E119")}),1.0]])]});
            var Q1;
            Q1=makeQuery(id+"F64.imprint","IMPRINT",FACE,{"disambiguationData":[TD([[makeQuery(id+"F64.imprint","IMPRINT",EDGE,{"derivedFrom":sQuery(id+"F64.wireOp",EDGE,"E113")}),1.0]])]});
            var Q2;
            Q2=makeQuery(id+"F64.imprint","IMPRINT",FACE,{"disambiguationData":[TD([[makeQuery(id+"F64.imprint","IMPRINT",EDGE,{"derivedFrom":sQuery(id+"F64.wireOp",EDGE,"E112.bottom")}),-1.0]])]});
            var Q3;
            Q3=makeQuery(id+"F64.imprint","IMPRINT",FACE,{"disambiguationData":[TD([[makeQuery(id+"F64.imprint","IMPRINT",EDGE,{"derivedFrom":sQuery(id+"F64.wireOp",EDGE,"E120")}),1.0]])]});
            var Q4;
            Q4=makeQuery(id+"F53.opExtrude","CAP_FACE",FACE,{"disambiguationData":[OSD([sQuery(id+"F52.wireOp",EDGE,"E99.0"),sQuery(id+"F52.wireOp",EDGE,"E102"),sQuery(id+"F52.wireOp",EDGE,"E103"),sQuery(id+"F52.wireOp",EDGE,"E104"),sQuery(id+"F52.wireOp",EDGE,"E105"),sQuery(id+"F52.wireOp",EDGE,"E106"),sQuery(id+"F52.wireOp",EDGE,"E107")])],"isStart":true});
            extrude(context, id + "F65", {"entities" : qUnion([Q0, Q1, Q2, Q3]), "operationType" : NewBodyOperationType.ADD, "endBound" : BoundingType.UP_TO_SURFACE, "endBoundEntityFace" : qUnion([Q4]), "depth" : 25 * mm});
        }
        {
            var Q0;
            Q0=makeQuery(id+"F64.imprint","IMPRINT",FACE,{"disambiguationData":[TD([[makeQuery(id+"F64.imprint","IMPRINT",EDGE,{"derivedFrom":sQuery(id+"F64.wireOp",EDGE,"E120")}),1.0]])]});
            var Q1;
            Q1=makeQuery(id+"F64.imprint","IMPRINT",FACE,{"disambiguationData":[TD([[makeQuery(id+"F64.imprint","IMPRINT",EDGE,{"derivedFrom":sQuery(id+"F64.wireOp",EDGE,"E119")}),1.0]])]});
            extrude(context, id + "F66", {"entities" : qUnion([Q0, Q1]), "operationType" : NewBodyOperationType.REMOVE, "endBound" : BoundingType.THROUGH_ALL, "oppositeDirection" : true, "depth" : 25 * mm, "hasSecondDirection" : true, "secondDirectionBound" : SecondDirectionBoundingType.THROUGH_ALL, "secondDirectionOppositeDirection" : false, "secondDirectionDepth" : 25 * mm});
        }
        {
            var Q0;
            Q0=makeQuery(id+"F53.opExtrude","SWEPT_BODY",BODY,{"disambiguationData":[OSD([sQuery(id+"F52.wireOp",EDGE,"E99.0"),sQuery(id+"F52.wireOp",EDGE,"E102"),sQuery(id+"F52.wireOp",EDGE,"E103"),sQuery(id+"F52.wireOp",EDGE,"E104"),sQuery(id+"F52.wireOp",EDGE,"E105"),sQuery(id+"F52.wireOp",EDGE,"E106"),sQuery(id+"F52.wireOp",EDGE,"E107")])]});
            var Q1;
            Q1=makeQuery(id+"F61.opExtrude","SWEPT_BODY",BODY,{"disambiguationData":[OSD([sQuery(id+"F60.wireOp",EDGE,"E110.0.0"),sQuery(id+"F60.wireOp",EDGE,"E110.0.1"),sQuery(id+"F60.wireOp",EDGE,"E110.0.2"),sQuery(id+"F60.wireOp",EDGE,"E110.0.3"),sQuery(id+"F60.wireOp",EDGE,"E110.0.4"),sQuery(id+"F60.wireOp",EDGE,"E110.0.5"),sQuery(id+"F60.wireOp",EDGE,"E110.0.6"),sQuery(id+"F60.wireOp",EDGE,"E110.0.7"),sQuery(id+"F60.wireOp",EDGE,"E110.0.8"),sQuery(id+"F60.wireOp",EDGE,"E110.0.9")])]});
            var Q2;
            Q2=makeQuery(id+"F41.opExtrude","SWEPT_BODY",BODY,{"disambiguationData":[OSD([sQuery(id+"F40.wireOp",EDGE,"E77.bottom"),sQuery(id+"F40.wireOp",EDGE,"E77.top"),sQuery(id+"F40.wireOp",EDGE,"E77.left"),sQuery(id+"F40.wireOp",EDGE,"E77.right"),sQuery(id+"F40.wireOp",EDGE,"E78.bottom"),sQuery(id+"F40.wireOp",EDGE,"E78.top"),sQuery(id+"F40.wireOp",EDGE,"E78.right")])]});
            var Q3;
            Q3=qCreatedBy(makeId("Right.planeOp"),FACE);
            mirror(context, id + "F67", {"entities" : qUnion([Q0, Q1, Q2]), "mirrorPlane" : qUnion([Q3])});
        }
        {
            var Q0;
            Q0=makeQuery(id+"F41.opExtrude","CAP_EDGE",EDGE,{"disambiguationData":[OSD([sQuery(id+"F40.wireOp",EDGE,"E77.right")])],"isStart":false});
            var Q1;
            Q1=makeQuery(id+"F41.opExtrude","CAP_EDGE",EDGE,{"disambiguationData":[OSD([sQuery(id+"F40.wireOp",EDGE,"E77.right")])],"isStart":true});
            var Q2;
            Q2=makeQuery(id+"F67.opPattern","COPY",EDGE,{"derivedFrom":makeQuery(id+"F41.opExtrude","CAP_EDGE",EDGE,{"disambiguationData":[OSD([sQuery(id+"F40.wireOp",EDGE,"E77.right")])],"isStart":true}),"instanceName":"1"});
            var Q3;
            Q3=makeQuery(id+"F67.opPattern","COPY",EDGE,{"derivedFrom":makeQuery(id+"F41.opExtrude","CAP_EDGE",EDGE,{"disambiguationData":[OSD([sQuery(id+"F40.wireOp",EDGE,"E77.right")])],"isStart":false}),"instanceName":"1"});
            chamfer(context, id + "F68", {"entities" : qUnion([Q0, Q1, Q2, Q3]), "chamferType" : ChamferType.TWO_OFFSETS, "width1" : 3 * mm, "oppositeDirection" : false, "width2" : 2 * mm, "tangentPropagation" : true});
        }
    });
